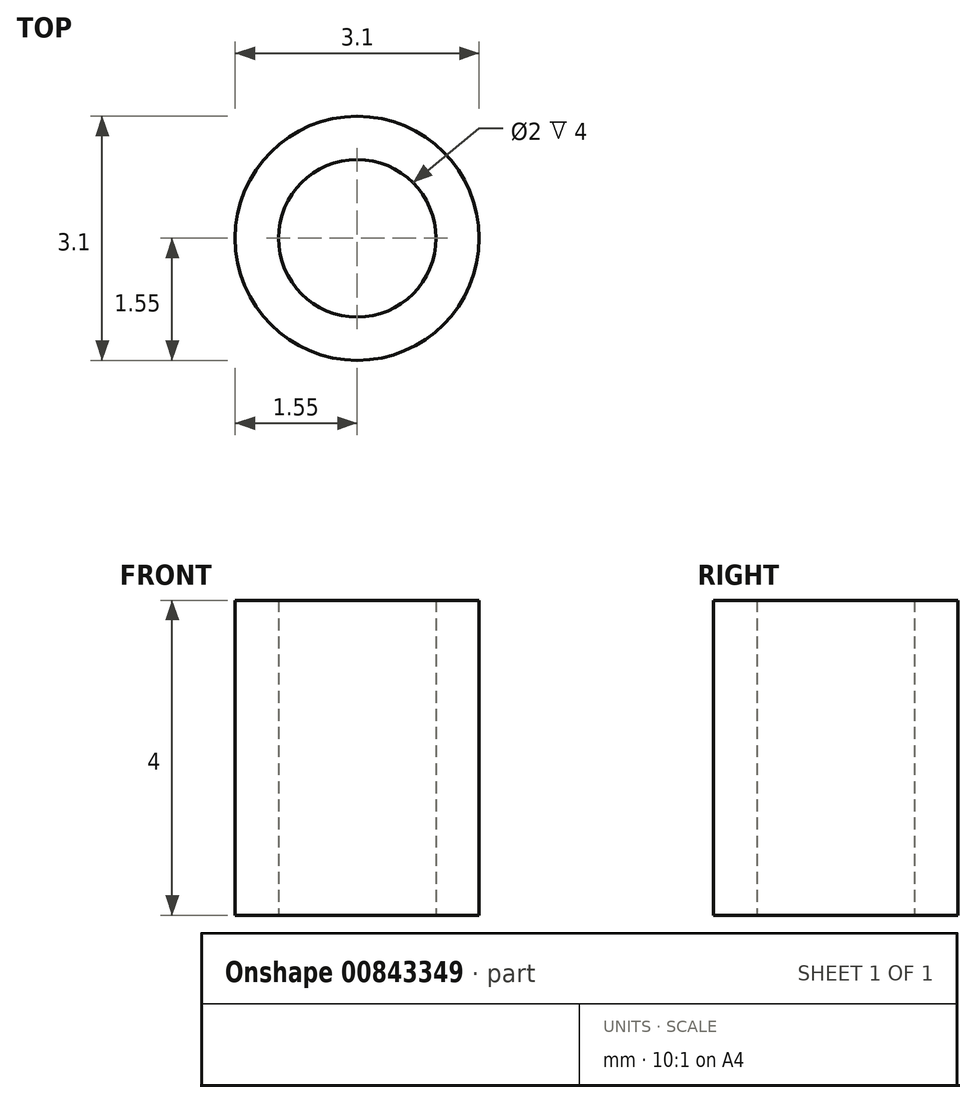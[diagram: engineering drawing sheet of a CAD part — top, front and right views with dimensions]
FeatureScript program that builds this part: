
annotation { "Feature Type Name" : "Feature", "Feature Type Description" : "" }
export const myFeature = defineFeature(function(context is Context, id is Id, definition is map)
    precondition{}
    {
        {
            var Q0;
            Q0=qCreatedBy(makeId("Top.planeOp"),FACE);
            var sketch = newSketch(context, id + "F0", { "sketchPlane" : qUnion([Q0])});
            skCircle(sketch, "E0", {"center": v(0, 0) * mm, "radius": 1 * mm});
            skCircle(sketch, "E1", {"center": v(0, 0) * mm, "radius": 1.55 * mm});
            skSolve(sketch);
        }
        {
            var Q0;
            Q0=makeQuery(id+"F0.imprint","IMPRINT",FACE,{"disambiguationData":[TD([[makeQuery(id+"F0.imprint","IMPRINT",EDGE,{"derivedFrom":sQuery(id+"F0.wireOp",EDGE,"E0")}),-1.0]])]});
            extrude(context, id + "F1", {"entities" : qUnion([Q0]), "depth" : 4 * mm, "offsetDistance" : 25 * mm});
        }
    });
